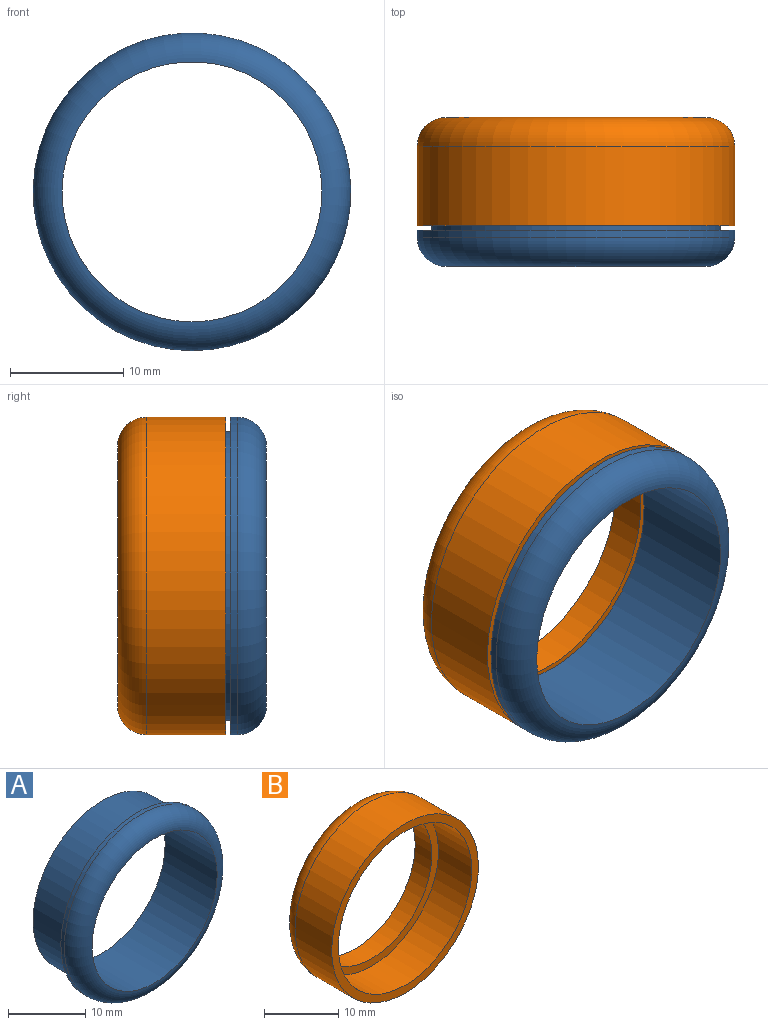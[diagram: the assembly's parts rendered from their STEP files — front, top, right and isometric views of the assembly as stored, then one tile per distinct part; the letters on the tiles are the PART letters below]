
ASSEMBLY  parts=2 mates=1
PART A: 6 faces, bbox 30.3x9.5x30.3 mm
  f0: cylinder r=14mm len=27.99mm, axis (0,1,0), area 55.8mm2, adj f1,f5
  f1: plane 27.99x27.99mm, normal (0,1,0), area 106.6mm2, adj f0,f2
  f2: cylinder r=12.73mm len=25.45mm, axis (0,1,0), area 507.7mm2, adj f1,f4
  f3: cylinder r=11.46mm len=22.91mm, axis (0,1,0), area 685.6mm2, adj f4,f5
  f4: plane 25.45x25.45mm, normal (0,1,0), area 96.5mm2, adj f2,f3
  f5: torus R=11.46mm, axis (0,-1,0), area 327.7mm2, adj f0,f3
PART B: 6 faces, bbox 30.3x9.5x30.3 mm
  f0: cylinder r=12.73mm len=25.45mm, axis (0,-1,0), area 507.7mm2, adj f2,f4
  f1: cylinder r=14mm len=27.99mm, axis (0,-1,0), area 614.2mm2, adj f2,f5
  f2: plane 27.99x27.99mm, normal (0,-1,0), area 106.6mm2, adj f0,f1
  f3: cylinder r=11.46mm len=22.91mm, axis (0,-1,0), area 228.5mm2, adj f4,f5
  f4: plane 25.45x25.45mm, normal (0,-1,0), area 96.5mm2, adj f0,f3
  f5: torus R=11.46mm, axis (0,-1,0), area 327.7mm2, adj f1,f3
PLACE A t=(0.33,6.79,10.73)mm
PLACE B rot(axis=(-0.82,-0.28,0.5),0deg) t=(0.33,7.21,10.73)mm
MATE slider A.f0 <-> B.f0  axis (0,-1,0) through (0.33,1.19,10.73)mm
